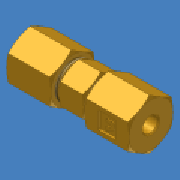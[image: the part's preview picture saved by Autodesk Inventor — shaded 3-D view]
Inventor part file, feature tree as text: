
AUTODESK INVENTOR PART (.ipt)
format: ipt  version: 2014 (Build 180170000, 170)  size: 288,256 bytes
history: native  units: in
note: dims shown in document units (in); Inventor stores cm internally (conversion verified against a paired STEP export)
features: other x2, sketch x1, imported_body x1
ambient origin geometry x8: Origin, YZ Plane, XZ Plane, XY Plane, X Axis, Y Axis, Z Axis, Center Point
bodies: Solid1 (feature_tree)
feature tree (4):
  other  "Table"
  other  "Union 62C.ipt"
  sketch  "Sketch1"
  imported_body  "DerivedBody::Union 62C.ipt"
